FCSTD DOCUMENT  (FreeCAD 0.16R6712 (Git))
Label: GearBoxDrawing
License: All rights reserved
LicenseURL: http://en.wikipedia.org/wiki/All_rights_reserved
objects: Sketcher::SketchObject×1
note: 1 computed .brp shape members not serialized (recipe doc carries the construction recipe); baked Part::Feature solids carry a one-line shape summary decoded from their .brp

FEATURE [Sketcher::SketchObject] Sketch
  sketch-geometry (115):
    g0: LineSegment StartX=0 StartY=50 StartZ=0 EndX=29 EndY=50 EndZ=0
    g1: LineSegment StartX=29 StartY=50 StartZ=0 EndX=29 EndY=-50 EndZ=0
    g2: LineSegment StartX=29 StartY=-50 StartZ=0 EndX=0 EndY=-50 EndZ=0
    g3: LineSegment StartX=0 StartY=-50 StartZ=0 EndX=0 EndY=50 EndZ=0
    g4: LineSegment StartX=29 StartY=40 StartZ=0 EndX=43 EndY=40 EndZ=0
    g5: LineSegment StartX=43 StartY=40 StartZ=0 EndX=43 EndY=-40 EndZ=0
    g6: LineSegment StartX=43 StartY=-40 StartZ=0 EndX=29 EndY=-40 EndZ=0
    g7: LineSegment StartX=29 StartY=-40 StartZ=0 EndX=29 EndY=40 EndZ=0
    g8: GeomPoint [constr] X=43 Y=0 Z=0
    g9: LineSegment StartX=43 StartY=40 StartZ=0 EndX=62 EndY=40 EndZ=0
    g10: LineSegment StartX=62 StartY=40 StartZ=0 EndX=62 EndY=-40 EndZ=0
    g11: LineSegment StartX=62 StartY=-40 StartZ=0 EndX=43 EndY=-40 EndZ=0
    g12: LineSegment StartX=43 StartY=-40 StartZ=0 EndX=43 EndY=40 EndZ=0
    g13: LineSegment StartX=43 StartY=20 StartZ=0 EndX=58 EndY=20 EndZ=0
    g14: LineSegment StartX=58 StartY=20 StartZ=0 EndX=58 EndY=-197.416 EndZ=0
    g15: LineSegment StartX=58 StartY=-197.416 StartZ=0 EndX=43 EndY=-197.416 EndZ=0
    g16: LineSegment StartX=43 StartY=-197.416 StartZ=0 EndX=43 EndY=20 EndZ=0
    g17: LineSegment StartX=43 StartY=6 StartZ=0 EndX=46 EndY=6 EndZ=0
    g18: LineSegment StartX=46 StartY=6 StartZ=0 EndX=48.8 EndY=3.2 EndZ=0
    g19: LineSegment StartX=48.8 StartY=3.2 StartZ=0 EndX=62 EndY=3.2 EndZ=0
    g20: LineSegment StartX=43 StartY=-6 StartZ=0 EndX=46 EndY=-6 EndZ=0
    g21: LineSegment StartX=46 StartY=-6 StartZ=0 EndX=48.8 EndY=-3.2 EndZ=0
    g22: LineSegment StartX=48.8 StartY=-3.2 StartZ=0 EndX=62 EndY=-3.2 EndZ=0
    g23: LineSegment StartX=48.8 StartY=3.2 StartZ=0 EndX=48.8 EndY=-3.2 EndZ=0
    g24: LineSegment StartX=46 StartY=6 StartZ=0 EndX=46 EndY=-6 EndZ=0
    g25: LineSegment StartX=63.5 StartY=41 StartZ=0 EndX=63.5 EndY=37 EndZ=0
    g26: LineSegment StartX=63.5 StartY=37 StartZ=0 EndX=68.5 EndY=37 EndZ=0
    g27: LineSegment StartX=68.5 StartY=37 StartZ=0 EndX=68.5 EndY=35.2 EndZ=0
    g28: LineSegment StartX=68.5 StartY=35.2 StartZ=0 EndX=71.5 EndY=35.2 EndZ=0
    g29: LineSegment StartX=71.5 StartY=35.2 StartZ=0 EndX=71.5 EndY=41 EndZ=0
    g30: LineSegment StartX=71.5 StartY=41 StartZ=0 EndX=63.5 EndY=41 EndZ=0
    g31: LineSegment StartX=63.5 StartY=27 StartZ=0 EndX=68.5 EndY=27 EndZ=0
    g32: LineSegment StartX=68.5 StartY=27 StartZ=0 EndX=68.5 EndY=28.8 EndZ=0
    g33: LineSegment StartX=68.5 StartY=28.8 StartZ=0 EndX=71.5 EndY=28.8 EndZ=0
    g34: LineSegment StartX=71.5 StartY=28.8 StartZ=0 EndX=71.5 EndY=7.5 EndZ=0
    g35: LineSegment StartX=63.5 StartY=8.6 StartZ=0 EndX=63.5 EndY=27 EndZ=0
    g36: LineSegment StartX=63.5 StartY=8.6 StartZ=0 EndX=63.5 EndY=-8.6 EndZ=0
    g37: LineSegment StartX=71.5 StartY=-7.5 StartZ=0 EndX=71.5 EndY=-10.6 EndZ=0
    g38: LineSegment StartX=71.5 StartY=-10.6 StartZ=0 EndX=63.5 EndY=-10.6 EndZ=0
    g39: LineSegment StartX=63.5 StartY=-10.6 StartZ=0 EndX=63.5 EndY=-8.6 EndZ=0
    g40: LineSegment StartX=63.5 StartY=8.6 StartZ=0 EndX=69.5 EndY=8.6 EndZ=0
    g41: LineSegment StartX=69.5 StartY=8.6 StartZ=0 EndX=69.5 EndY=-8.6 EndZ=0
    g42: LineSegment StartX=69.5 StartY=-8.6 StartZ=0 EndX=63.5 EndY=-8.6 EndZ=0
    g43: LineSegment StartX=71.5 StartY=7.5 StartZ=0 EndX=69.5 EndY=7.5 EndZ=0
    g44: LineSegment StartX=69.5 StartY=7.5 StartZ=0 EndX=69.5 EndY=8.6 EndZ=0
    g45: LineSegment StartX=69.5 StartY=8.6 StartZ=0 EndX=63.5 EndY=8.6 EndZ=0
    g46: LineSegment StartX=71.5 StartY=-7.5 StartZ=0 EndX=69.5 EndY=-7.5 EndZ=0
    g47: LineSegment StartX=69.5 StartY=-7.5 StartZ=0 EndX=69.5 EndY=-8.6 EndZ=0
    g48: LineSegment StartX=69.5 StartY=-8.6 StartZ=0 EndX=63.5 EndY=-8.6 EndZ=0
    g49: LineSegment [constr] StartX=71.5 StartY=35.2 StartZ=0 EndX=71.5 EndY=28.8 EndZ=0
    g50: LineSegment [constr] StartX=68.5 StartY=35.2 StartZ=0 EndX=68.5 EndY=28.8 EndZ=0
    g51: LineSegment [constr] StartX=63.5 StartY=37 StartZ=0 EndX=63.5 EndY=27 EndZ=0
    g52: LineSegment [constr] StartX=63.5 StartY=8.6 StartZ=0 EndX=63.5 EndY=-8.6 EndZ=0
    g53: LineSegment [constr] StartX=71.5 StartY=7.5 StartZ=0 EndX=71.5 EndY=-7.5 EndZ=0
    g54: GeomPoint [constr] X=71.5 Y=0 Z=0
    g55: GeomPoint [constr] X=71.5 Y=32 Z=0
    g56: GeomPoint [constr] X=63.5 Y=32 Z=0
    g57: LineSegment [constr] StartX=63.5 StartY=32 StartZ=0 EndX=71.5 EndY=32 EndZ=0
    g58: GeomPoint [constr] X=63.5 Y=0 Z=0
    g59: LineSegment [constr] StartX=63.5 StartY=0 StartZ=0 EndX=71.5 EndY=0 EndZ=0
    g60: LineSegment StartX=63.5 StartY=6 StartZ=0 EndX=62 EndY=6 EndZ=0
    g61: LineSegment StartX=62 StartY=6 StartZ=0 EndX=62 EndY=-6 EndZ=0
    g62: LineSegment StartX=62 StartY=-6 StartZ=0 EndX=63.5 EndY=-6 EndZ=0
    g63: LineSegment StartX=63.5 StartY=-6 StartZ=0 EndX=63.5 EndY=6 EndZ=0
    g64: LineSegment StartX=63.5 StartY=-6 StartZ=0 EndX=63.5 EndY=6 EndZ=0
    g65: GeomPoint [constr] X=63.5 Y=0 Z=0
    g66: LineSegment StartX=71.5 StartY=38 StartZ=0 EndX=74.5 EndY=38 EndZ=0
    g67: LineSegment StartX=74.5 StartY=38 StartZ=0 EndX=74.5 EndY=26 EndZ=0
    g68: LineSegment StartX=74.5 StartY=26 StartZ=0 EndX=71.5 EndY=26 EndZ=0
    g69: LineSegment StartX=71.5 StartY=26 StartZ=0 EndX=71.5 EndY=38 EndZ=0
    g70: LineSegment StartX=62 StartY=3.2 StartZ=0 EndX=76 EndY=3.2 EndZ=0
    g71: LineSegment StartX=76 StartY=3.2 StartZ=0 EndX=76 EndY=-3.2 EndZ=0
    g72: LineSegment StartX=76 StartY=-3.2 StartZ=0 EndX=62 EndY=-3.2 EndZ=0
    g73: LineSegment [constr] StartX=46 StartY=0 StartZ=0 EndX=76 EndY=0 EndZ=0
    g74: GeomPoint [constr] X=48.8 Y=0 Z=0
    g75: LineSegment StartX=69.5 StartY=6 StartZ=0 EndX=71 EndY=6 EndZ=0
    g76: LineSegment StartX=71 StartY=6 StartZ=0 EndX=71 EndY=-6 EndZ=0
    g77: LineSegment StartX=71 StartY=-6 StartZ=0 EndX=69.5 EndY=-6 EndZ=0
    g78: LineSegment StartX=69.5 StartY=-6 StartZ=0 EndX=69.5 EndY=6 EndZ=0
    g79: GeomPoint [constr] X=69.5 Y=0 Z=0
    g80: LineSegment StartX=71 StartY=6 StartZ=0 EndX=76 EndY=6 EndZ=0
    g81: LineSegment StartX=76 StartY=6 StartZ=0 EndX=76 EndY=-6 EndZ=0
    g82: LineSegment StartX=76 StartY=-6 StartZ=0 EndX=71 EndY=-6 EndZ=0
    g83: LineSegment StartX=71 StartY=-6 StartZ=0 EndX=71 EndY=6 EndZ=0
    g84: GeomPoint [constr] X=71 Y=0 Z=0
    g85: LineSegment StartX=74.5 StartY=44.5 StartZ=0 EndX=85.5 EndY=44.5 EndZ=0
    g86: LineSegment StartX=85.5 StartY=44.5 StartZ=0 EndX=85.5 EndY=3.5 EndZ=0
    g87: LineSegment StartX=85.5 StartY=3.5 StartZ=0 EndX=74.5 EndY=3.5 EndZ=0
    g88: LineSegment StartX=74.5 StartY=3.5 StartZ=0 EndX=74.5 EndY=44.5 EndZ=0
    g89: LineSegment [constr] StartX=74.5 StartY=32 StartZ=0 EndX=85.5 EndY=32 EndZ=0
    g90: LineSegment StartX=83 StartY=3.5 StartZ=0 EndX=77 EndY=3.5 EndZ=0
    g91: LineSegment StartX=77 StartY=3.5 StartZ=0 EndX=77 EndY=-196.963 EndZ=0
    g92: LineSegment StartX=77 StartY=-196.963 StartZ=0 EndX=83 EndY=-196.963 EndZ=0
    g93: LineSegment StartX=83 StartY=-196.963 StartZ=0 EndX=83 EndY=3.5 EndZ=0
    g94: GeomPoint [constr] X=80 Y=3.5 Z=0
    g95: LineSegment StartX=85.5 StartY=38 StartZ=0 EndX=86 EndY=38 EndZ=0
    g96: LineSegment StartX=86 StartY=38 StartZ=0 EndX=86 EndY=26 EndZ=0
    g97: LineSegment StartX=86 StartY=26 StartZ=0 EndX=85.5 EndY=26 EndZ=0
    g98: LineSegment StartX=85.5 StartY=26 StartZ=0 EndX=85.5 EndY=38 EndZ=0
    g99: LineSegment StartX=86 StartY=39 StartZ=0 EndX=93 EndY=39 EndZ=0
    g100: LineSegment StartX=93 StartY=39 StartZ=0 EndX=93 EndY=-39 EndZ=0
    g101: LineSegment StartX=93 StartY=-39 StartZ=0 EndX=86 EndY=-39 EndZ=0
    g102: LineSegment StartX=86 StartY=-39 StartZ=0 EndX=86 EndY=39 EndZ=0
    g103: GeomPoint [constr] X=86 Y=32 Z=0
    g104: LineSegment StartX=93 StartY=-40 StartZ=0 EndX=107 EndY=-40 EndZ=0
    g105: LineSegment StartX=107 StartY=-40 StartZ=0 EndX=107 EndY=40 EndZ=0
    g106: LineSegment StartX=107 StartY=40 StartZ=0 EndX=93 EndY=40 EndZ=0
    g107: LineSegment StartX=93 StartY=40 StartZ=0 EndX=93 EndY=-40 EndZ=0
    g108: GeomPoint [constr] X=93 Y=0 Z=0
    g109: LineSegment StartX=107 StartY=-50 StartZ=0 EndX=136 EndY=-50 EndZ=0
    g110: LineSegment StartX=136 StartY=-50 StartZ=0 EndX=136 EndY=50 EndZ=0
    g111: LineSegment StartX=136 StartY=50 StartZ=0 EndX=107 EndY=50 EndZ=0
    g112: LineSegment StartX=107 StartY=50 StartZ=0 EndX=107 EndY=-50 EndZ=0
    g113: GeomPoint [constr] X=107 Y=48.1972 Z=0
    g114: GeomPoint [constr] X=107 Y=0 Z=0
  constraints (314):
    c: Coincident(g0,g1)
    c: Coincident(g1,g2)
    c: Coincident(g2,g3)
    c: Coincident(g3,g0)
    c: Horizontal(g0)
    c: Horizontal(g2)
    c: Vertical(g1)
    c: Vertical(g3)
    c: PointOnObject(g0,g-2)
    c: Symmetric(g2,g0,g-1)
    c: DistanceY(g3,g3) = 100
    c: DistanceX(g0,g0) = 29
    c: Coincident(g4,g5)
    c: Coincident(g5,g6)
    c: Coincident(g6,g7)
    c: Coincident(g7,g4)
    c: Horizontal(g4)
    c: Horizontal(g6)
    c: Vertical(g5)
    c: Vertical(g7)
    c: PointOnObject(g4,g1)
    c: DistanceX(g4,g4) = 14
    c: DistanceY(g5,g5) = 80
    c: PointOnObject(g8,g-1)
    c: Symmetric(g4,g5,g8)
    c: Coincident(g9,g10)
    c: Coincident(g10,g11)
    c: Coincident(g11,g12)
    c: Coincident(g12,g9)
    c: Horizontal(g9)
    c: Horizontal(g11)
    c: Vertical(g10)
    c: Vertical(g12)
    c: Coincident(g9,g4)
    c: DistanceX(g9,g9) = 19
    c: Coincident(g11,g5)
    c: Coincident(g13,g14)
    c: Coincident(g14,g15)
    c: Coincident(g15,g16)
    c: Coincident(g16,g13)
    c: Horizontal(g13)
    c: Horizontal(g15)
    c: Vertical(g14)
    c: Vertical(g16)
    c: PointOnObject(g13,g5)
    c: DistanceX(g13,g13) = 15
    c: DistanceY(g8,g13) = 20
    c: PointOnObject(g17,g5)
    c: Horizontal(g17)
    c: Coincident(g17,g18)
    c: Coincident(g18,g19)
    c: PointOnObject(g19,g10)
    c: Horizontal(g19)
    c: PointOnObject(g20,g5)
    c: Coincident(g20,g21)
    c: Coincident(g21,g22)
    c: PointOnObject(g22,g10)
    c: Horizontal(g22)
    c: Horizontal(g20)
    c: DistanceY(g22,g19) = 6.4
    c: Coincident(g23,g18)
    c: Coincident(g23,g21)
    c: Vertical(g23)
    c: Coincident(g24,g17)
    c: Coincident(g24,g20)
    c: Vertical(g24)
    c: Angle(g21,g24) = 0.785398
    c: Angle(g24,g18) = 0.785398
    c: Symmetric(g20,g17,g8)
    c: DistanceX(g20,g20) = 3
    c: Vertical(g25)
    c: Coincident(g25,g26)
    c: Horizontal(g26)
    c: Coincident(g26,g27)
    c: Vertical(g27)
    c: Coincident(g27,g28)
    c: Horizontal(g28)
    c: Coincident(g28,g29)
    c: Vertical(g29)
    c: Coincident(g29,g30)
    c: Coincident(g30,g25)
    c: Horizontal(g30)
    c: Horizontal(g31)
    c: Coincident(g31,g32)
    c: Vertical(g32)
    c: Coincident(g32,g33)
    c: Horizontal(g33)
    c: Coincident(g33,g34)
    c: Vertical(g34)
    c: Coincident(g35,g31)
    c: Vertical(g35)
    c: Vertical(g36)
    c: Vertical(g37)
    c: Coincident(g37,g38)
    c: Horizontal(g38)
    c: Coincident(g38,g39)
    c: Vertical(g39)
    c: Coincident(g40,g41)
    c: Coincident(g41,g42)
    c: Horizontal(g40)
    c: Horizontal(g42)
    c: Vertical(g41)
    c: Coincident(g42,g36)
    c: Coincident(g40,g36)
    c: Coincident(g34,g43)
    c: Horizontal(g43)
    c: Coincident(g43,g44)
    c: Coincident(g44,g40)
    c: Coincident(g44,g45)
    c: Coincident(g45,g35)
    c: Horizontal(g45)
    c: PointOnObject(g43,g41)
    c: Coincident(g37,g46)
    c: Horizontal(g46)
    c: Coincident(g46,g47)
    c: Coincident(g47,g41)
    c: Vertical(g47)
    c: Coincident(g47,g48)
    c: Coincident(g48,g39)
    c: Horizontal(g48)
    c: Coincident(g49,g33)
    c: Vertical(g49)
    c: Coincident(g28,g49)
    c: Coincident(g50,g27)
    c: Coincident(g50,g32)
    c: Vertical(g50)
    c: Coincident(g51,g25)
    c: Vertical(g51)
    c: Coincident(g51,g31)
    c: Coincident(g52,g35)
    c: Coincident(g52,g39)
    c: Vertical(g52)
    c: Coincident(g53,g34)
    c: Coincident(g53,g37)
    c: Vertical(g53)
    c: PointOnObject(g54,g53)
    c: Symmetric(g37,g34,g54)
    c: Symmetric(g28,g33,g55)
    c: DistanceY(g53,g53) = 15
    c: DistanceY(g49,g49) = 6.4
    c: DistanceY(g37,g54) = 10.6
    c: DistanceY(g55,g29) = 9
    c: PointOnObject(g56,g51)
    c: Symmetric(g25,g31,g56)
    c: DistanceY(g56,g25) = 5
    c: Coincident(g57,g56)
    c: Coincident(g57,g55)
    c: Horizontal(g57)
    c: PointOnObject(g58,g52)
    c: Symmetric(g35,g39,g58)
    c: DistanceY(g39,g58) = 8.6
    c: Coincident(g59,g58)
    c: Coincident(g59,g54)
    c: Horizontal(g59)
    c: Coincident(g60,g61)
    c: Coincident(g61,g62)
    c: Coincident(g62,g63)
    c: Coincident(g63,g60)
    c: Horizontal(g60)
    c: Horizontal(g62)
    c: Vertical(g61)
    c: Vertical(g63)
    c: PointOnObject(g60,g36)
    c: DistanceX(g60,g60) = 1.5
    c: DistanceX(g40,g40) = 6
    c: Vertical(g64)
    c: PointOnObject(g54,g-1)
    c: PointOnObject(g65,g36)
    c: Symmetric(g60,g62,g65)
    c: PointOnObject(g65,g59)
    c: DistanceY(g61,g61) = 12
    c: PointOnObject(g60,g10)
    c: DistanceX(g43,g43) = 2
    c: DistanceX(g38,g38) = 8
    c: DistanceX(g26,g26) = 5
    c: Coincident(g66,g67)
    c: Coincident(g67,g68)
    c: Coincident(g68,g69)
    c: Coincident(g69,g66)
    c: Horizontal(g66)
    c: Horizontal(g68)
    c: Vertical(g67)
    c: Vertical(g69)
    c: PointOnObject(g66,g29)
    c: DistanceX(g66,g66) = 3
    c: DistanceY(g67,g67) = 12
    c: Symmetric(g66,g68,g55)
    c: DistanceY(g54,g55) = 32
    c: Coincident(g19,g70)
    c: Horizontal(g70)
    c: Coincident(g70,g71)
    c: Vertical(g71)
    c: Coincident(g71,g72)
    c: Coincident(g72,g22)
    c: Horizontal(g72)
    c: PointOnObject(g73,g71)
    c: Horizontal(g73)
    c: PointOnObject(g73,g24)
    c: PointOnObject(g74,g73)
    c: PointOnObject(g74,g23)
    c: DistanceY(g24,g24) = 12
    c: DistanceX(g73,g73) = 30
    c: Coincident(g75,g76)
    c: Coincident(g76,g77)
    c: Coincident(g77,g78)
    c: Coincident(g78,g75)
    c: Horizontal(g75)
    c: Horizontal(g77)
    c: Vertical(g76)
    c: Vertical(g78)
    c: PointOnObject(g75,g41)
    c: DistanceX(g75,g75) = 1.5
    c: PointOnObject(g73,g-1)
    c: PointOnObject(g79,g41)
    c: PointOnObject(g79,g-1)
    c: Symmetric(g75,g77,g79)
    c: DistanceY(g76,g76) = 12
    c: Coincident(g80,g81)
    c: Coincident(g81,g82)
    c: Coincident(g82,g83)
    c: Coincident(g83,g80)
    c: Horizontal(g80)
    c: Horizontal(g82)
    c: Vertical(g81)
    c: Vertical(g83)
    c: PointOnObject(g80,g76)
    c: DistanceX(g80,g80) = 5
    c: DistanceY(g81,g81) = 12
    c: PointOnObject(g84,g76)
    c: Symmetric(g80,g82,g84)
    c: PointOnObject(g84,g-1)
    c: Horizontal(g85)
    c: Coincident(g85,g86)
    c: Vertical(g86)
    c: Coincident(g86,g87)
    c: Horizontal(g87)
    c: Coincident(g87,g88)
    c: Coincident(g88,g85)
    c: Vertical(g88)
    c: DistanceX(g85,g85) = 11
    c: DistanceY(g86,g86) = 41
    c: PointOnObject(g89,g86)
    c: Horizontal(g89)
    c: DistanceY(g89,g85) = 12.5
    c: Symmetric(g66,g67,g89)
    c: Coincident(g90,g91)
    c: Coincident(g91,g92)
    c: Coincident(g92,g93)
    c: Coincident(g93,g90)
    c: Horizontal(g90)
    c: Horizontal(g92)
    c: Vertical(g91)
    c: Vertical(g93)
    c: PointOnObject(g90,g87)
    c: Symmetric(g87,g86,g94)
    c: Symmetric(g90,g90,g94)
    c: DistanceX(g92,g92) = 6
    c: PointOnObject(g89,g88)
    c: Coincident(g95,g96)
    c: Coincident(g96,g97)
    c: Coincident(g97,g98)
    c: Coincident(g98,g95)
    c: Horizontal(g95)
    c: Horizontal(g97)
    c: Vertical(g96)
    c: Vertical(g98)
    c: Symmetric(g95,g97,g89)
    c: Equal(g96,g67)
    c: DistanceX(g95,g95) = 0.5
    c: Coincident(g99,g100)
    c: Coincident(g100,g101)
    c: Coincident(g101,g102)
    c: Coincident(g102,g99)
    c: Horizontal(g99)
    c: Horizontal(g101)
    c: Vertical(g100)
    c: Vertical(g102)
    c: PointOnObject(g99,g96)
    c: DistanceX(g99,g99) = 7
    c: PointOnObject(g103,g96)
    c: Symmetric(g95,g96,g103)
    c: DistanceY(g103,g99) = 7
    c: DistanceY(g100,g100) = 78
    c: Coincident(g104,g105)
    c: Coincident(g105,g106)
    c: Coincident(g106,g107)
    c: Coincident(g107,g104)
    c: Horizontal(g104)
    c: Horizontal(g106)
    c: Vertical(g105)
    c: Vertical(g107)
    c: PointOnObject(g104,g100)
    c: PointOnObject(g108,g107)
    c: Symmetric(g106,g104,g108)
    c: Symmetric(g100,g99,g108)
    c: DistanceY(g105,g105) = 80
    c: DistanceX(g106,g106) = 14
    c: Coincident(g109,g110)
    c: Coincident(g110,g111)
    c: Coincident(g111,g112)
    c: Coincident(g112,g109)
    c: Horizontal(g109)
    c: Horizontal(g111)
    c: Vertical(g110)
    c: Vertical(g112)
    c: PointOnObject(g113,g105)
    c: DistanceY(g110,g110) = 100
    c: PointOnObject(g114,g112)
    c: Symmetric(g111,g109,g114)
    c: Symmetric(g105,g104,g114)
    c: DistanceX(g111,g111) = 29
    c: DistanceX(g0,g110) = 136
    c: DistanceX(g4,g99) = 50
    c: DistanceX(g9,g85) = 12.5
